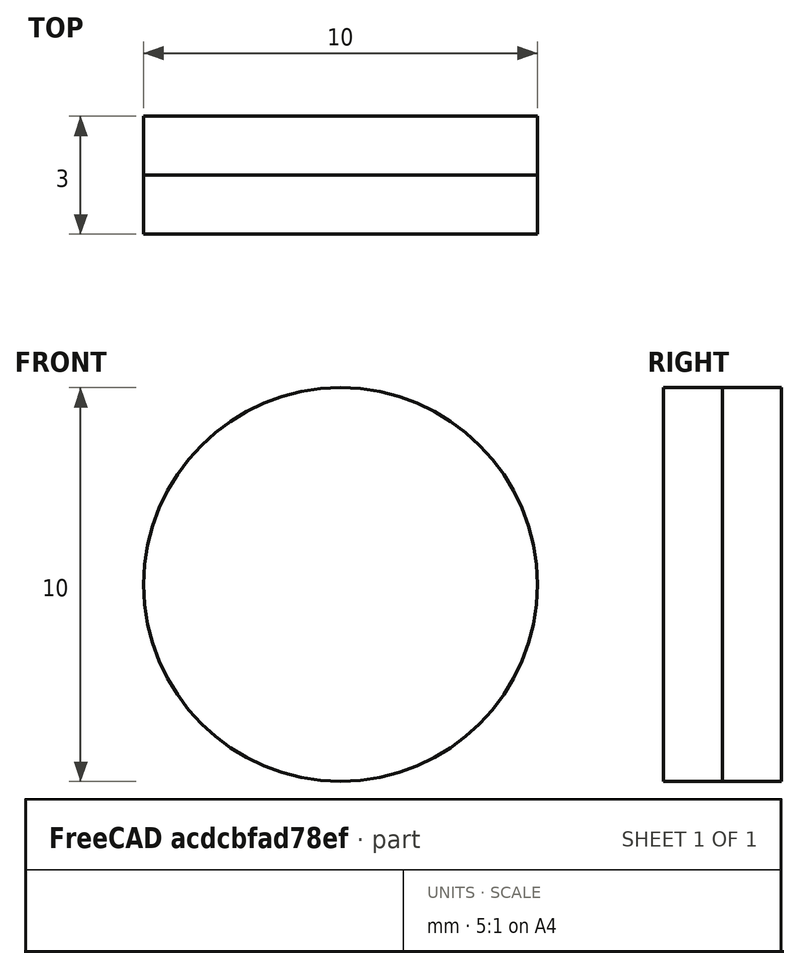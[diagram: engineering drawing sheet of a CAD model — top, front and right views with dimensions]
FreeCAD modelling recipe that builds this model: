
FCSTD DOCUMENT  (FreeCAD 0.21R33771 (Git))
Label: Magnet
License: Public Domain
LicenseURL: https://en.wikipedia.org/wiki/Public_domain
objects: App::Part×3, Part::Cylinder×2, PartDesign::CoordinateSystem×1
note: 3 computed .brp shape members not serialized (recipe doc carries the construction recipe); baked Part::Feature solids carry a one-line shape summary decoded from their .brp

FEATURE [Part::Cylinder] Cylinder  label="SouthMagPole"
  Angle = 360
  AttacherType = Attacher::AttachEngine3D
  FirstAngle = 0
  Height = 1.5
  Placement = pos=(0,0,0) rot=(1,0,0;1.5708rad)
  Radius = 5
  SecondAngle = 0
FEATURE [App::Part] Part001  label="South Pole"
  Group = -> [Cylinder]
  Origin = -> Origin001
FEATURE [Part::Cylinder] Cylinder001  label="NorthMagPole"
  Angle = 360
  AttacherType = Attacher::AttachEngine3D
  FirstAngle = 0
  Height = 1.5
  Placement = pos=(0,-1.5,2e-16) rot=(1,0,0;1.5708rad)
  Radius = 5
  SecondAngle = 0
FEATURE [App::Part] Part002  label="North Pole"
  Group = -> [Cylinder001]
  Origin = -> Origin002
FEATURE [PartDesign::CoordinateSystem] AP  label="Magnet AP"
  AttacherType = Attacher::AttachEngine3D
  AttachmentOffset = pos=(0,0,0) rot=(-0.57735,0.57735,-0.57735;2.0944rad)
  MapMode = 11
  Placement = pos=(0,-1.5,0) rot=(0,0,1;0rad)
  Support = -> [Cylinder]
FEATURE [App::Part] Part  label="Magnet"
  Group = -> [Part001,Part002,AP]
  Origin = -> Origin
  Placement = pos=(-8e-16,-1.5,0) rot=(0,0,1;3.14159rad)
